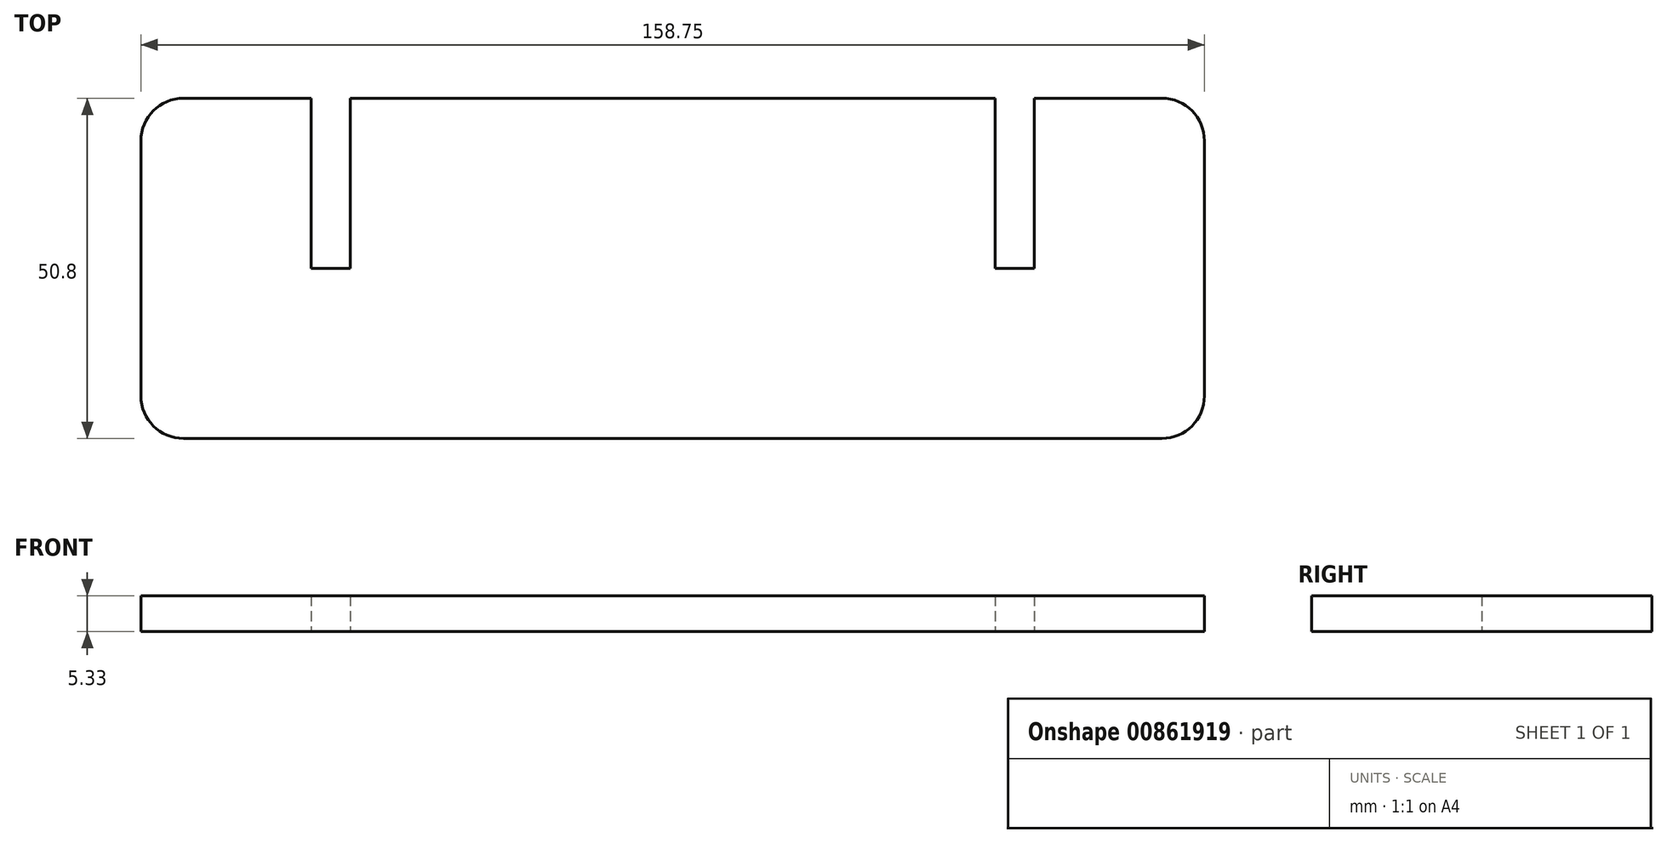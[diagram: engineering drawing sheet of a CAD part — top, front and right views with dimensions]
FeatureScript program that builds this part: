
annotation { "Feature Type Name" : "Feature", "Feature Type Description" : "" }
export const myFeature = defineFeature(function(context is Context, id is Id, definition is map)
    precondition{}
    {
        {
            var Q0;
            Q0=qCreatedBy(makeId("Top.planeOp"),FACE);
            var sketch = newSketch(context, id + "F0", { "sketchPlane" : qUnion([Q0])});
            skLineSegment(sketch, "E0.bottom", {"start": v(-110.75, 15.72) * mm, "end": v(-91.7, 15.72) * mm});
            skLineSegment(sketch, "E0.top", {"start": v(-110.75, -35.08) * mm, "end": v(35.3, -35.08) * mm});
            skLineSegment(sketch, "E0.left", {"start": v(-117.1, 9.37) * mm, "end": v(-117.1, -28.73) * mm});
            skLineSegment(sketch, "E0.right", {"start": v(41.65, 9.37) * mm, "end": v(41.65, -28.73) * mm});
            skLineSegment(sketch, "E1.top", {"start": v(-91.7, -9.68) * mm, "end": v(-85.86, -9.68) * mm});
            skLineSegment(sketch, "E1.left", {"start": v(-91.7, 15.72) * mm, "end": v(-91.7, -9.68) * mm});
            skLineSegment(sketch, "E1.right", {"start": v(-85.86, 15.72) * mm, "end": v(-85.86, -9.68) * mm});
            skLineSegment(sketch, "E2.top", {"start": v(10.4, -9.68) * mm, "end": v(16.25, -9.68) * mm});
            skLineSegment(sketch, "E2.left", {"start": v(10.4, 15.72) * mm, "end": v(10.4, -9.68) * mm});
            skLineSegment(sketch, "E2.right", {"start": v(16.25, 15.72) * mm, "end": v(16.25, -9.68) * mm});
            skLineSegment(sketch, "E3.trimOffspring", {"start": v(-85.86, 15.72) * mm, "end": v(10.4, 15.72) * mm});
            skLineSegment(sketch, "E4.trimOffspring", {"start": v(16.25, 15.72) * mm, "end": v(35.3, 15.72) * mm});
            skPoint(sketch, "E5.visualSharp", {"position": v(-117.1, 15.72) * mm});
            skArc(sketch, "E5.filletArc", {"start": v(-110.75, 15.72) * mm, "mid": v(-115.24, 13.86) * mm, "end": v(-117.1, 9.37) * mm});
            skPoint(sketch, "E6.visualSharp", {"position": v(-117.1, -35.08) * mm});
            skArc(sketch, "E6.filletArc", {"start": v(-117.1, -28.73) * mm, "mid": v(-115.24, -33.22) * mm, "end": v(-110.75, -35.08) * mm});
            skPoint(sketch, "E7.visualSharp", {"position": v(41.65, 15.72) * mm});
            skArc(sketch, "E7.filletArc", {"start": v(41.65, 9.37) * mm, "mid": v(39.79, 13.86) * mm, "end": v(35.3, 15.72) * mm});
            skPoint(sketch, "E8.visualSharp", {"position": v(41.65, -35.08) * mm});
            skArc(sketch, "E8.filletArc", {"start": v(35.3, -35.08) * mm, "mid": v(39.79, -33.22) * mm, "end": v(41.65, -28.73) * mm});
            skSolve(sketch);
        }
        {
            var Q0;
            Q0 = qSketchRegion(id + "F0", true);
            extrude(context, id + "F1", {"entities" : qUnion([Q0]), "depth" : 5.33 * mm, "offsetDistance" : 25.4 * mm});
        }
    });
